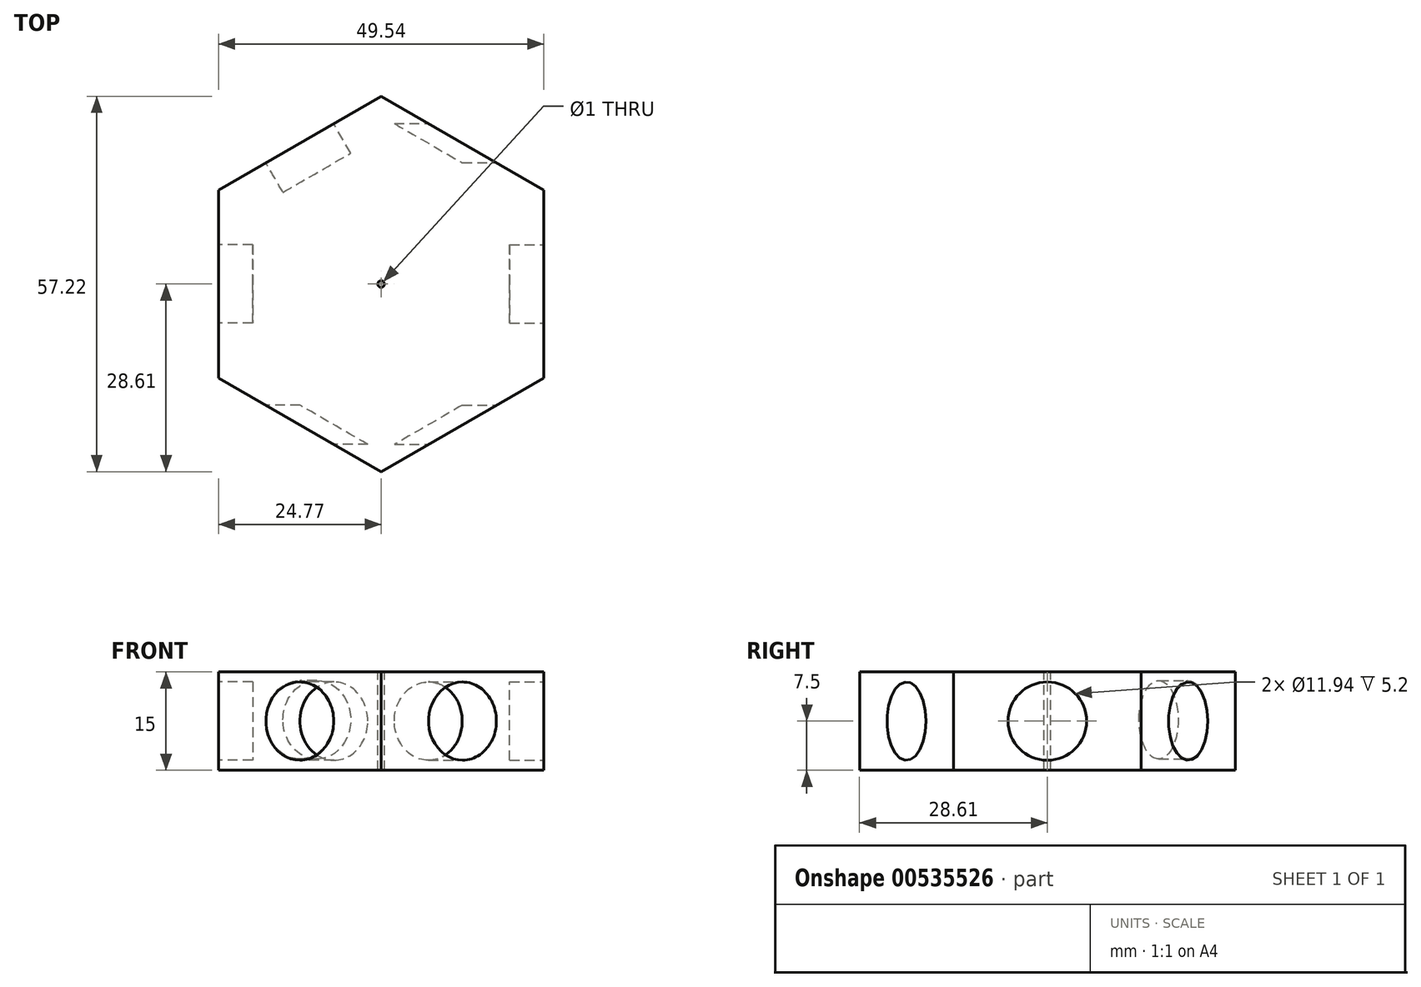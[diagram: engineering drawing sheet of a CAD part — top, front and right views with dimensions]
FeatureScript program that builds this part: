
annotation { "Feature Type Name" : "Feature", "Feature Type Description" : "" }
export const myFeature = defineFeature(function(context is Context, id is Id, definition is map)
    precondition{}
    {
        {
            var Q0;
            Q0=qCreatedBy(makeId("Top.planeOp"),FACE);
            var sketch = newSketch(context, id + "F0", { "sketchPlane" : qUnion([Q0])});
            skCircle(sketch, "E0.cCircle", {"center": v(0, 0) * mm, "radius": 24.77 * mm, "construction": true});
            skLineSegment(sketch, "E0.0", {"start": v(24.77, -14.3) * mm, "end": v(0, -28.6) * mm});
            skLineSegment(sketch, "E0.1", {"start": v(0, -28.6) * mm, "end": v(-24.77, -14.3) * mm});
            skLineSegment(sketch, "E0.2", {"start": v(-24.77, -14.3) * mm, "end": v(-24.77, 14.3) * mm});
            skLineSegment(sketch, "E0.3", {"start": v(-24.77, 14.3) * mm, "end": v(0, 28.6) * mm});
            skLineSegment(sketch, "E0.4", {"start": v(0, 28.6) * mm, "end": v(24.77, 14.3) * mm});
            skLineSegment(sketch, "E0.5", {"start": v(24.77, 14.3) * mm, "end": v(24.77, -14.3) * mm});
            skPoint(sketch, "E0.0.midPoint", {"position": v(12.39, -21.46) * mm});
            skSolve(sketch);
        }
        {
            var Q0;
            Q0=makeQuery(id+"F0.imprint","IMPRINT",FACE,{"disambiguationData":[TD([[makeQuery(id+"F0.imprint","IMPRINT",EDGE,{"derivedFrom":sQuery(id+"F0.wireOp",EDGE,"E0.0")}),-1.0]])]});
            extrude(context, id + "F1", {"entities" : qUnion([Q0]), "depth" : 15 * mm, "offsetDistance" : 25 * mm});
        }
        {
            var Q0;
            Q0=makeQuery(id+"F1.opExtrude","SWEPT_FACE",FACE,{"disambiguationData":[OSD([sQuery(id+"F0.wireOp",EDGE,"E0.3")])]});
            var sketch = newSketch(context, id + "F2", { "sketchPlane" : qUnion([Q0])});
            skCircle(sketch, "E1", {"center": v(0, 7.7) * mm, "radius": 5.97 * mm});
            skSolve(sketch);
        }
        {
            var Q0;
            Q0=makeQuery(id+"F2.imprint","IMPRINT",FACE,{"disambiguationData":[TD([[makeQuery(id+"F2.imprint","IMPRINT",EDGE,{"derivedFrom":sQuery(id+"F2.wireOp",EDGE,"E1")}),1.0]])]});
            extrude(context, id + "F3", {"entities" : qUnion([Q0]), "operationType" : NewBodyOperationType.REMOVE, "oppositeDirection" : true, "depth" : 5.2 * mm, "offsetDistance" : 25 * mm});
        }
        {
            var Q0;
            Q0=makeQuery(id+"F1.opExtrude","SWEPT_FACE",FACE,{"disambiguationData":[OSD([sQuery(id+"F0.wireOp",EDGE,"E0.2")])]});
            var sketch = newSketch(context, id + "F4", { "sketchPlane" : qUnion([Q0])});
            skCircle(sketch, "E2", {"center": v(0, 7.5) * mm, "radius": 5.97 * mm});
            skSolve(sketch);
        }
        {
            var Q0;
            Q0=makeQuery(id+"F1.opExtrude","SWEPT_FACE",FACE,{"disambiguationData":[OSD([sQuery(id+"F0.wireOp",EDGE,"E0.1")])]});
            var sketch = newSketch(context, id + "F5", { "sketchPlane" : qUnion([Q0])});
            skCircle(sketch, "E3", {"center": v(0, 7.5) * mm, "radius": 5.97 * mm});
            skSolve(sketch);
        }
        {
            var Q0;
            Q0=makeQuery(id+"F1.opExtrude","SWEPT_FACE",FACE,{"disambiguationData":[OSD([sQuery(id+"F0.wireOp",EDGE,"E0.0")])]});
            var sketch = newSketch(context, id + "F6", { "sketchPlane" : qUnion([Q0])});
            skCircle(sketch, "E4", {"center": v(0, 7.5) * mm, "radius": 5.97 * mm});
            skSolve(sketch);
        }
        {
            var Q0;
            Q0=makeQuery(id+"F1.opExtrude","SWEPT_FACE",FACE,{"disambiguationData":[OSD([sQuery(id+"F0.wireOp",EDGE,"E0.5")])]});
            var sketch = newSketch(context, id + "F7", { "sketchPlane" : qUnion([Q0])});
            skCircle(sketch, "E5", {"center": v(0, 7.5) * mm, "radius": 5.97 * mm});
            skSolve(sketch);
        }
        {
            var Q0;
            Q0=makeQuery(id+"F1.opExtrude","SWEPT_FACE",FACE,{"disambiguationData":[OSD([sQuery(id+"F0.wireOp",EDGE,"E0.4")])]});
            var sketch = newSketch(context, id + "F8", { "sketchPlane" : qUnion([Q0])});
            skCircle(sketch, "E6", {"center": v(0, 7.5) * mm, "radius": 5.97 * mm});
            skSolve(sketch);
        }
        {
            var Q0;
            Q0 = qSketchRegion(id + "F7", true);
            var Q1;
            Q1 = qSketchRegion(id + "F6", true);
            var Q2;
            Q2 = qSketchRegion(id + "F5", true);
            var Q3;
            Q3 = qSketchRegion(id + "F4", true);
            var Q4;
            Q4 = qSketchRegion(id + "F8", true);
            extrude(context, id + "F9", {"entities" : qUnion([Q0, Q1, Q2, Q3, Q4]), "operationType" : NewBodyOperationType.REMOVE, "oppositeDirection" : true, "depth" : 5.2 * mm, "offsetDistance" : 25 * mm});
        }
        {
            var Q0;
            Q0=makeQuery(id+"F1.opExtrude","SWEPT_FACE",FACE,{"disambiguationData":[OSD([sQuery(id+"F0.wireOp",EDGE,"E0.2")])]});
            var sketch = newSketch(context, id + "F10", { "sketchPlane" : qUnion([Q0])});
            skCircle(sketch, "E7", {"center": v(0, 7.5) * mm, "radius": 5.97 * mm});
            skSolve(sketch);
        }
        {
            var Q0;
            Q0=makeQuery(id+"F1.opExtrude","SWEPT_FACE",FACE,{"disambiguationData":[OSD([sQuery(id+"F0.wireOp",EDGE,"E0.1")])]});
            var sketch = newSketch(context, id + "F11", { "sketchPlane" : qUnion([Q0])});
            skCircle(sketch, "E8", {"center": v(0, 7.5) * mm, "radius": 5.97 * mm});
            skSolve(sketch);
        }
        {
            var Q0;
            Q0=makeQuery(id+"F10.imprint","IMPRINT",FACE,{"disambiguationData":[TD([[makeQuery(id+"F10.imprint","IMPRINT",EDGE,{"derivedFrom":sQuery(id+"F10.wireOp",EDGE,"E7")}),1.0]])]});
            var Q1;
            Q1=makeQuery(id+"F11.imprint","IMPRINT",FACE,{"disambiguationData":[TD([[makeQuery(id+"F11.imprint","IMPRINT",EDGE,{"derivedFrom":sQuery(id+"F11.wireOp",EDGE,"E8")}),1.0]])]});
            extrude(context, id + "F12", {"entities" : qUnion([Q0, Q1]), "operationType" : NewBodyOperationType.REMOVE, "oppositeDirection" : true, "depth" : 5.2 * mm, "offsetDistance" : 25 * mm});
        }
        {
            var Q0;
            Q0=makeQuery(id+"F1.opExtrude","CAP_FACE",FACE,{"disambiguationData":[OSD([sQuery(id+"F0.wireOp",EDGE,"E0.0"),sQuery(id+"F0.wireOp",EDGE,"E0.1"),sQuery(id+"F0.wireOp",EDGE,"E0.2"),sQuery(id+"F0.wireOp",EDGE,"E0.3"),sQuery(id+"F0.wireOp",EDGE,"E0.4"),sQuery(id+"F0.wireOp",EDGE,"E0.5")])],"isStart":false});
            var sketch = newSketch(context, id + "F13", { "sketchPlane" : qUnion([Q0])});
            skCircle(sketch, "E9", {"center": v(0, 0) * mm, "radius": 0.5 * mm});
            skSolve(sketch);
        }
        {
            var Q0;
            Q0=makeQuery(id+"F13.imprint","IMPRINT",FACE,{"disambiguationData":[TD([[makeQuery(id+"F13.imprint","IMPRINT",EDGE,{"derivedFrom":sQuery(id+"F13.wireOp",EDGE,"E9")}),1.0]])]});
            extrude(context, id + "F14", {"entities" : qUnion([Q0]), "operationType" : NewBodyOperationType.REMOVE, "oppositeDirection" : true, "depth" : 25 * mm, "offsetDistance" : 25 * mm});
        }
    });
